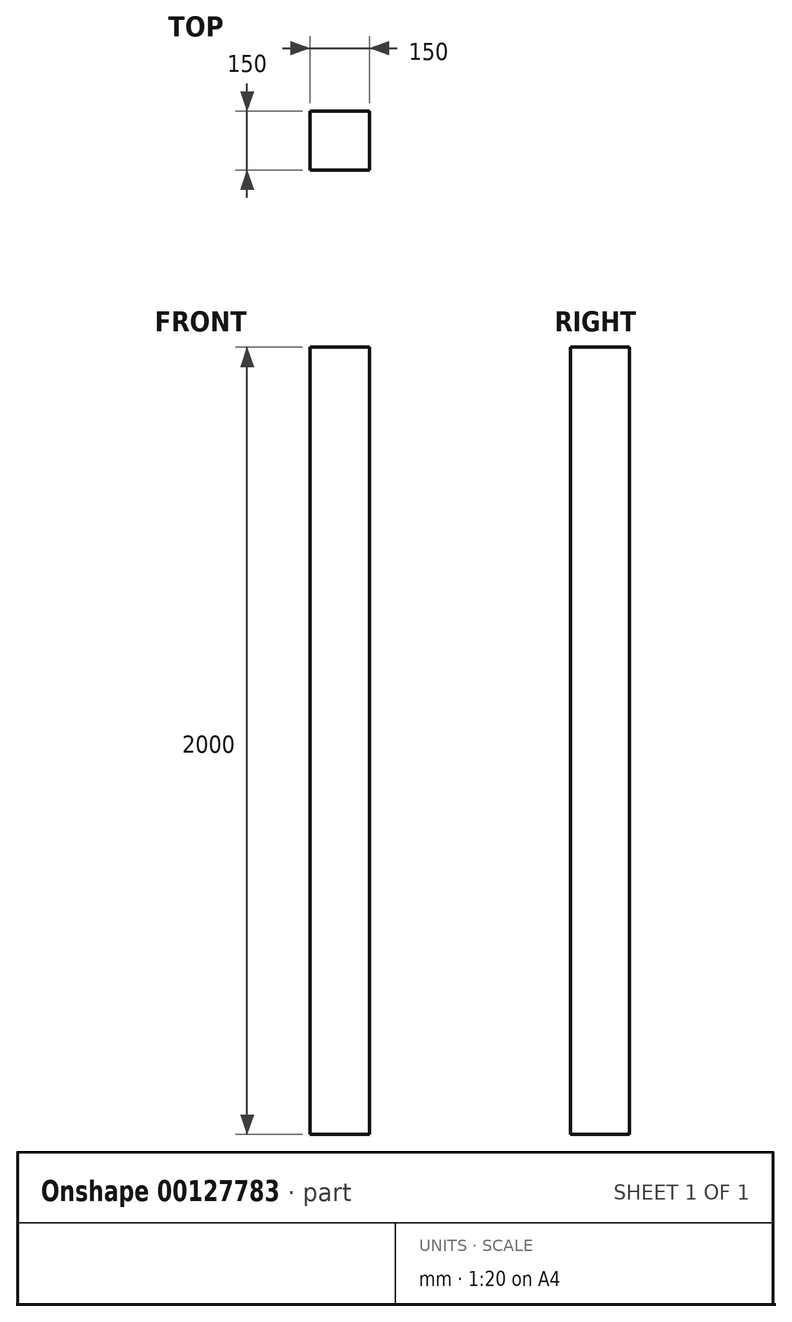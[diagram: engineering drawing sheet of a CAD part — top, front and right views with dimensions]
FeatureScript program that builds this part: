
annotation { "Feature Type Name" : "Feature", "Feature Type Description" : "" }
export const myFeature = defineFeature(function(context is Context, id is Id, definition is map)
    precondition{}
    {
        {
            var Q0;
            Q0=qCreatedBy(makeId("Top.planeOp"),FACE);
            var sketch = newSketch(context, id + "F0", { "sketchPlane" : qUnion([Q0])});
            skLineSegment(sketch, "E0.bottom", {"start": v(-75, 75) * mm, "end": v(75, 75) * mm});
            skLineSegment(sketch, "E0.top", {"start": v(-75, -75) * mm, "end": v(75, -75) * mm});
            skLineSegment(sketch, "E0.left", {"start": v(-75, 75) * mm, "end": v(-75, -75) * mm});
            skLineSegment(sketch, "E0.right", {"start": v(75, 75) * mm, "end": v(75, -75) * mm});
            skPoint(sketch, "E0.middle", {"position": v(0, 0) * mm});
            skSolve(sketch);
        }
        {
            var Q0;
            Q0 = qSketchRegion(id + "F0", true);
            extrude(context, id + "F1", {"entities" : qUnion([Q0]), "endBound" : BoundingType.SYMMETRIC, "depth" : 2000 * mm});
        }
    });
